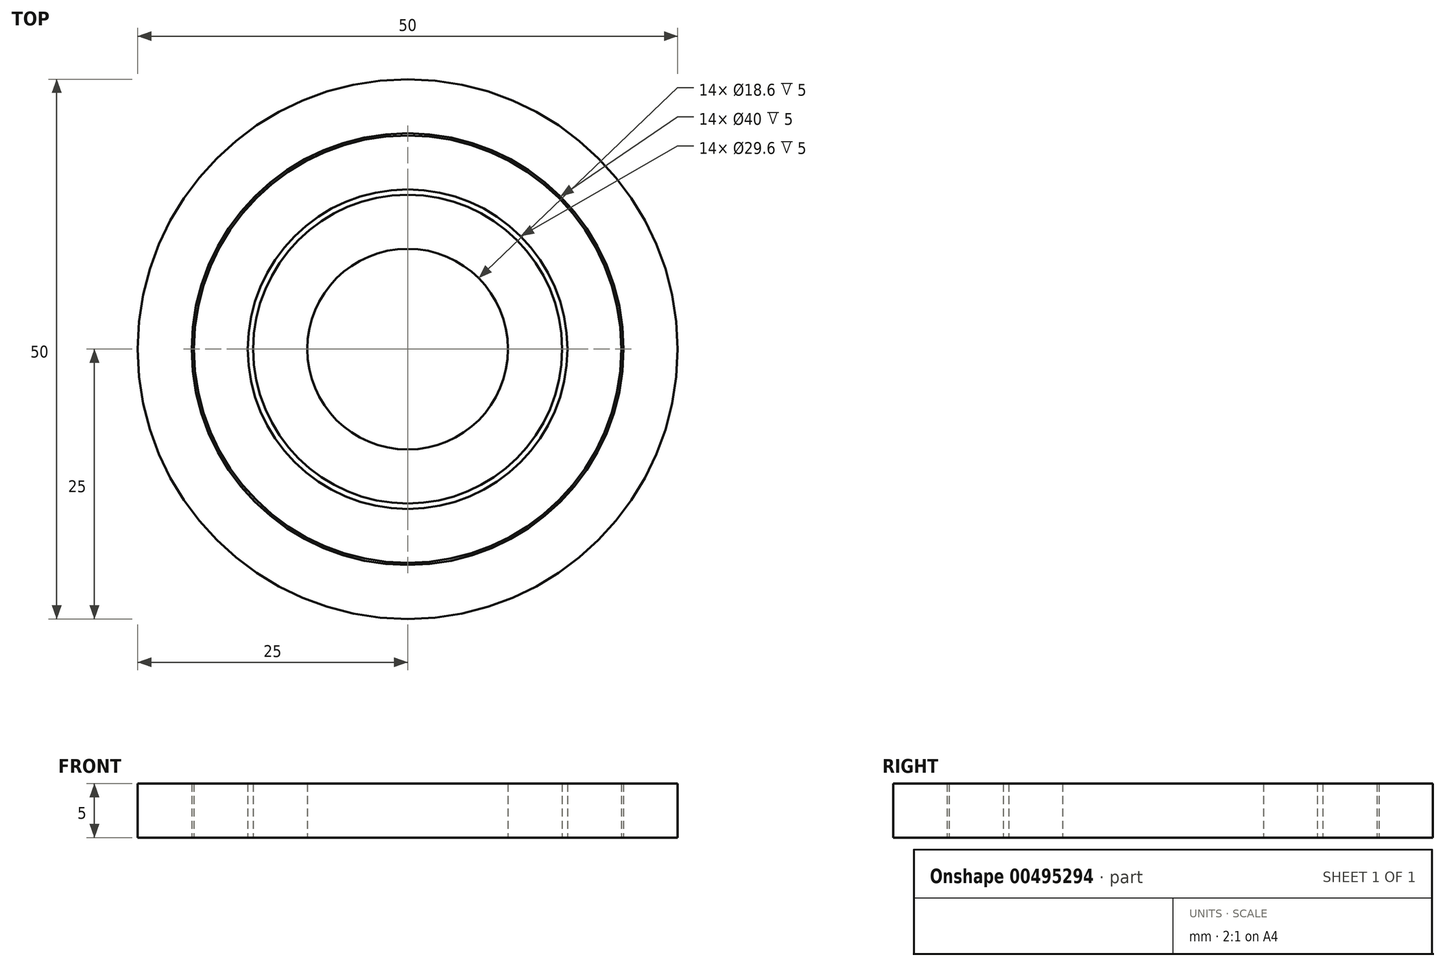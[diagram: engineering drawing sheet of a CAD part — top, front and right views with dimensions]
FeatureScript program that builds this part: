
annotation { "Feature Type Name" : "Feature", "Feature Type Description" : "" }
export const myFeature = defineFeature(function(context is Context, id is Id, definition is map)
    precondition{}
    {
        {
            var Q0;
            Q0=qCreatedBy(makeId("Top.planeOp"),FACE);
            var sketch = newSketch(context, id + "F0", { "sketchPlane" : qUnion([Q0])});
            skCircle(sketch, "E0", {"center": v(0, 0) * mm, "radius": 25 * mm});
            skCircle(sketch, "E1", {"center": v(0, 0) * mm, "radius": 20 * mm});
            skCircle(sketch, "E2", {"center": v(0, 0) * mm, "radius": 19.8 * mm});
            skCircle(sketch, "E3", {"center": v(0, 0) * mm, "radius": 14.8 * mm});
            skCircle(sketch, "E4", {"center": v(0, 0) * mm, "radius": 14.3 * mm});
            skCircle(sketch, "E5", {"center": v(0, 0) * mm, "radius": 9.3 * mm});
            skSolve(sketch);
        }
        {
            var Q0;
            Q0=makeQuery(id+"F0.imprint","IMPRINT",FACE,{"disambiguationData":[TD([[makeQuery(id+"F0.imprint","IMPRINT",EDGE,{"derivedFrom":sQuery(id+"F0.wireOp",EDGE,"E0")}),1.0]])]});
            var Q1;
            Q1=makeQuery(id+"F0.imprint","IMPRINT",FACE,{"disambiguationData":[TD([[makeQuery(id+"F0.imprint","IMPRINT",EDGE,{"derivedFrom":sQuery(id+"F0.wireOp",EDGE,"E2")}),1.0]])]});
            var Q2;
            Q2=makeQuery(id+"F0.imprint","IMPRINT",FACE,{"disambiguationData":[TD([[makeQuery(id+"F0.imprint","IMPRINT",EDGE,{"derivedFrom":sQuery(id+"F0.wireOp",EDGE,"E4")}),1.0]])]});
            extrude(context, id + "F1", {"entities" : qUnion([Q0, Q1, Q2]), "depth" : 5 * mm, "offsetDistance" : 25 * mm});
        }
    });
